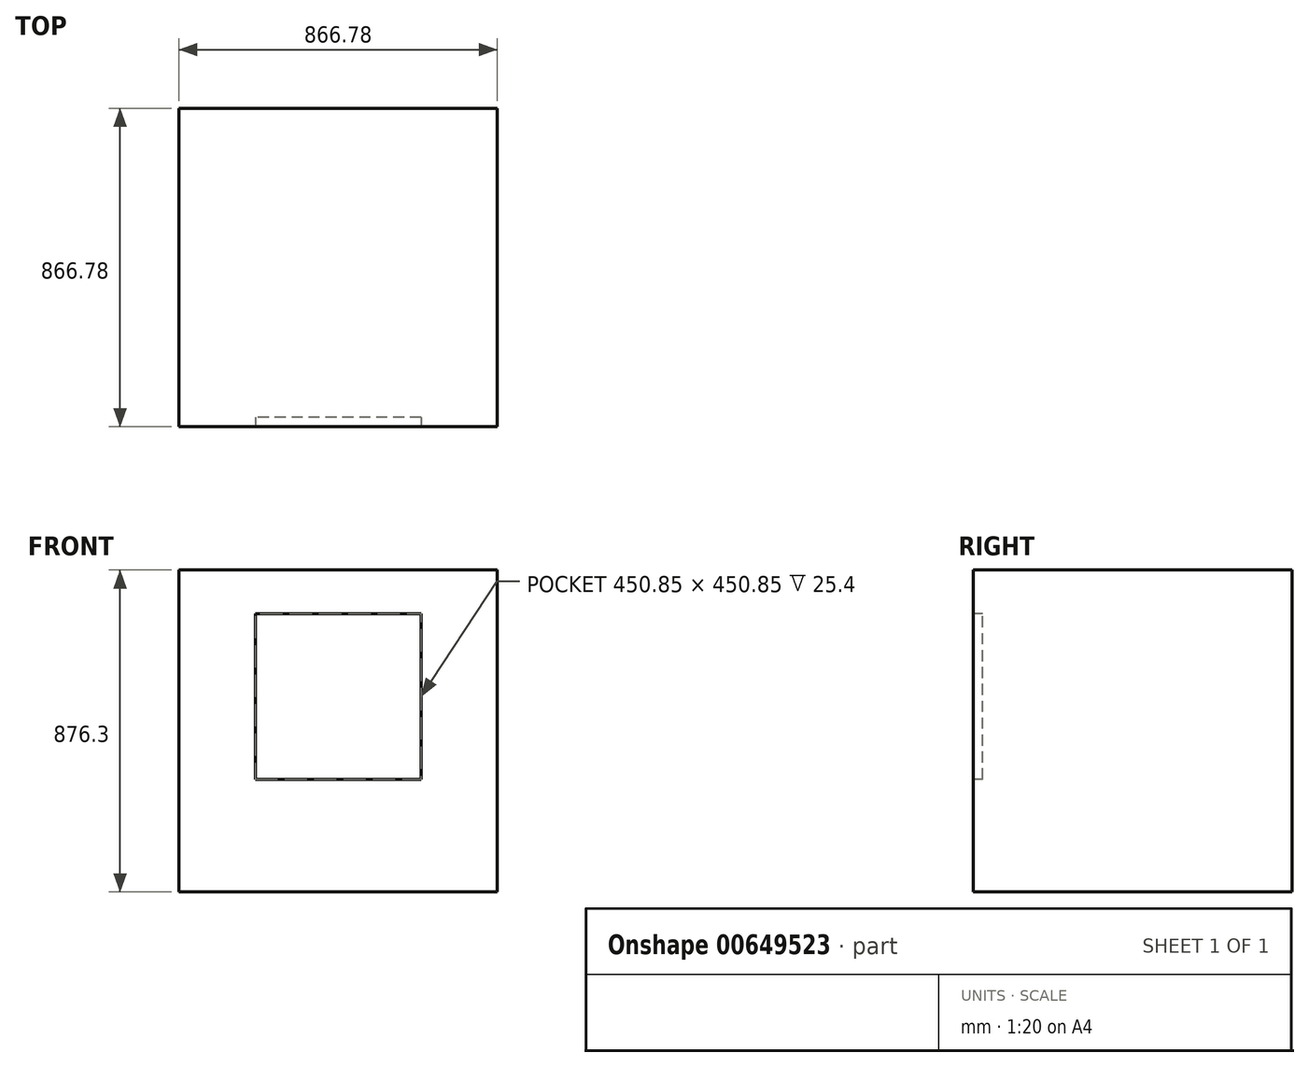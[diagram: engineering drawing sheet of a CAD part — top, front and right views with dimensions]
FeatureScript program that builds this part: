
annotation { "Feature Type Name" : "Feature", "Feature Type Description" : "" }
export const myFeature = defineFeature(function(context is Context, id is Id, definition is map)
    precondition{}
    {
        {
            var Q0;
            Q0=qCreatedBy(makeId("Top.planeOp"),FACE);
            var sketch = newSketch(context, id + "F0", { "sketchPlane" : qUnion([Q0])});
            skLineSegment(sketch, "E0.bottom", {"start": v(433.39, -433.39) * mm, "end": v(-433.39, -433.39) * mm});
            skLineSegment(sketch, "E0.top", {"start": v(433.39, 433.39) * mm, "end": v(-433.39, 433.39) * mm});
            skLineSegment(sketch, "E0.left", {"start": v(433.39, -433.39) * mm, "end": v(433.39, 433.39) * mm});
            skLineSegment(sketch, "E0.right", {"start": v(-433.39, -433.39) * mm, "end": v(-433.39, 433.39) * mm});
            skPoint(sketch, "E0.middle", {"position": v(0, 0) * mm});
            skSolve(sketch);
        }
        {
            var Q0;
            Q0 = qSketchRegion(id + "F0", true);
            var Q1;
            Q1 = qConstructionFilter(qBodyType(qCreatedBy(id + "F0" ,EDGE), BodyType.WIRE), ConstructionObject.NO);
            extrude(context, id + "F1", {"entities" : qUnion([Q0]), "surfaceEntities" : qUnion([Q1]), "depth" : 876.3 * mm, "offsetDistance" : 25.4 * mm});
        }
        {
            var Q0;
            Q0=makeQuery(id+"F1.opExtrude","SWEPT_FACE",FACE,{"disambiguationData":[OSD([sQuery(id+"F0.wireOp",EDGE,"E0.bottom")])]});
            var sketch = newSketch(context, id + "F2", { "sketchPlane" : qUnion([Q0])});
            skLineSegment(sketch, "E1.bottom", {"start": v(225.42, 306.39) * mm, "end": v(-225.43, 306.39) * mm});
            skLineSegment(sketch, "E1.top", {"start": v(225.43, 757.24) * mm, "end": v(-225.42, 757.24) * mm});
            skLineSegment(sketch, "E1.left", {"start": v(225.43, 306.39) * mm, "end": v(225.43, 757.24) * mm});
            skLineSegment(sketch, "E1.right", {"start": v(-225.43, 306.39) * mm, "end": v(-225.43, 757.24) * mm});
            skPoint(sketch, "E1.middle", {"position": v(0, 531.81) * mm});
            skSolve(sketch);
        }
        {
            var Q0;
            Q0 = qSketchRegion(id + "F2", true);
            extrude(context, id + "F3", {"entities" : qUnion([Q0]), "operationType" : NewBodyOperationType.REMOVE, "oppositeDirection" : true, "depth" : 25.4 * mm, "offsetDistance" : 25.4 * mm});
        }
    });
